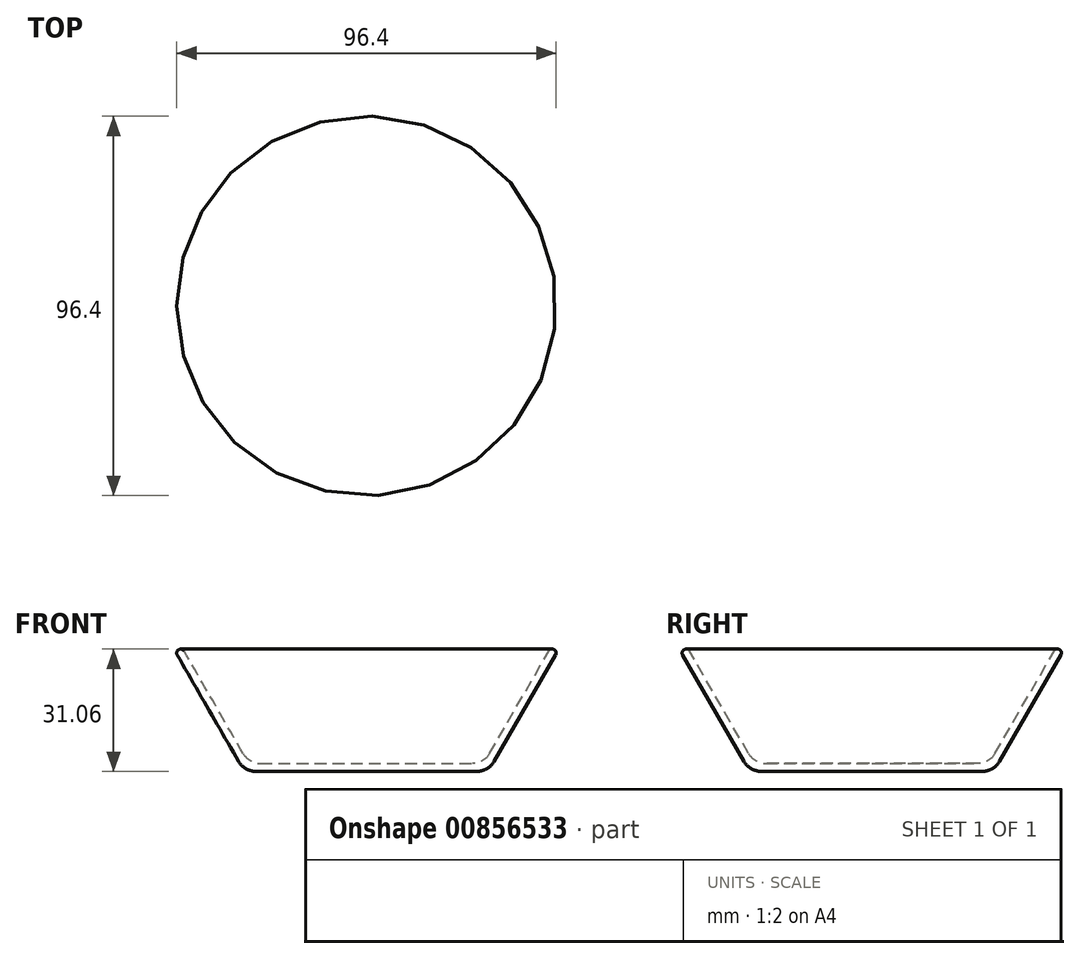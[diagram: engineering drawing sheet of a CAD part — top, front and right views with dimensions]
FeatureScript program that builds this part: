
annotation { "Feature Type Name" : "Feature", "Feature Type Description" : "" }
export const myFeature = defineFeature(function(context is Context, id is Id, definition is map)
    precondition{}
    {
        {
            var Q0;
            Q0=qCreatedBy(makeId("Front.planeOp"),FACE);
            var sketch = newSketch(context, id + "F0", { "sketchPlane" : qUnion([Q0])});
            skLineSegment(sketch, "E0", {"start": v(0, 0) * mm, "end": v(26.96, 0) * mm});
            skLineSegment(sketch, "E1", {"start": v(31.29, 2.5) * mm, "end": v(46.33, 28.56) * mm});
            skLineSegment(sketch, "E2.0", {"start": v(32.44, 0.5) * mm, "end": v(48.06, 27.56) * mm});
            skLineSegment(sketch, "E2.1", {"start": v(0, -2) * mm, "end": v(28.11, -2) * mm});
            skLineSegment(sketch, "E3", {"start": v(47.81, 28.85) * mm, "end": v(47.81, 28.85) * mm});
            skLineSegment(sketch, "E4", {"start": v(0, -2) * mm, "end": v(0, 47.87) * mm});
            skPoint(sketch, "E5.visualSharp", {"position": v(31, -2) * mm});
            skArc(sketch, "E5.filletArc", {"start": v(28.11, -2) * mm, "mid": v(30.61, -1.33) * mm, "end": v(32.44, 0.5) * mm});
            skPoint(sketch, "E6.visualSharp", {"position": v(29.85, 0) * mm});
            skArc(sketch, "E6.filletArc", {"start": v(26.96, 0) * mm, "mid": v(29.46, 0.67) * mm, "end": v(31.29, 2.5) * mm});
            skPoint(sketch, "E7.visualSharp", {"position": v(48.5, 28.31) * mm});
            skArc(sketch, "E7.filletArc", {"start": v(48.06, 27.56) * mm, "mid": v(48.18, 28.25) * mm, "end": v(47.81, 28.85) * mm});
            skPoint(sketch, "E8.visualSharp", {"position": v(46.9, 29.55) * mm});
            skArc(sketch, "E8.filletArc", {"start": v(47.81, 28.85) * mm, "mid": v(47, 29.04) * mm, "end": v(46.33, 28.56) * mm});
            skSolve(sketch);
        }
        {
            var Q0;
            Q0 = qSketchRegion(id + "F0", true);
            var Q1;
            Q1=sQuery(id+"F0.wireOp",EDGE,"E4");
            revolve(context, id + "F1", {"surfaceOperationType" : NewSurfaceOperationType.NEW, "entities" : qUnion([Q0]), "axis" : qUnion([Q1]), "revolveType" : RevolveType.FULL});
        }
    });
